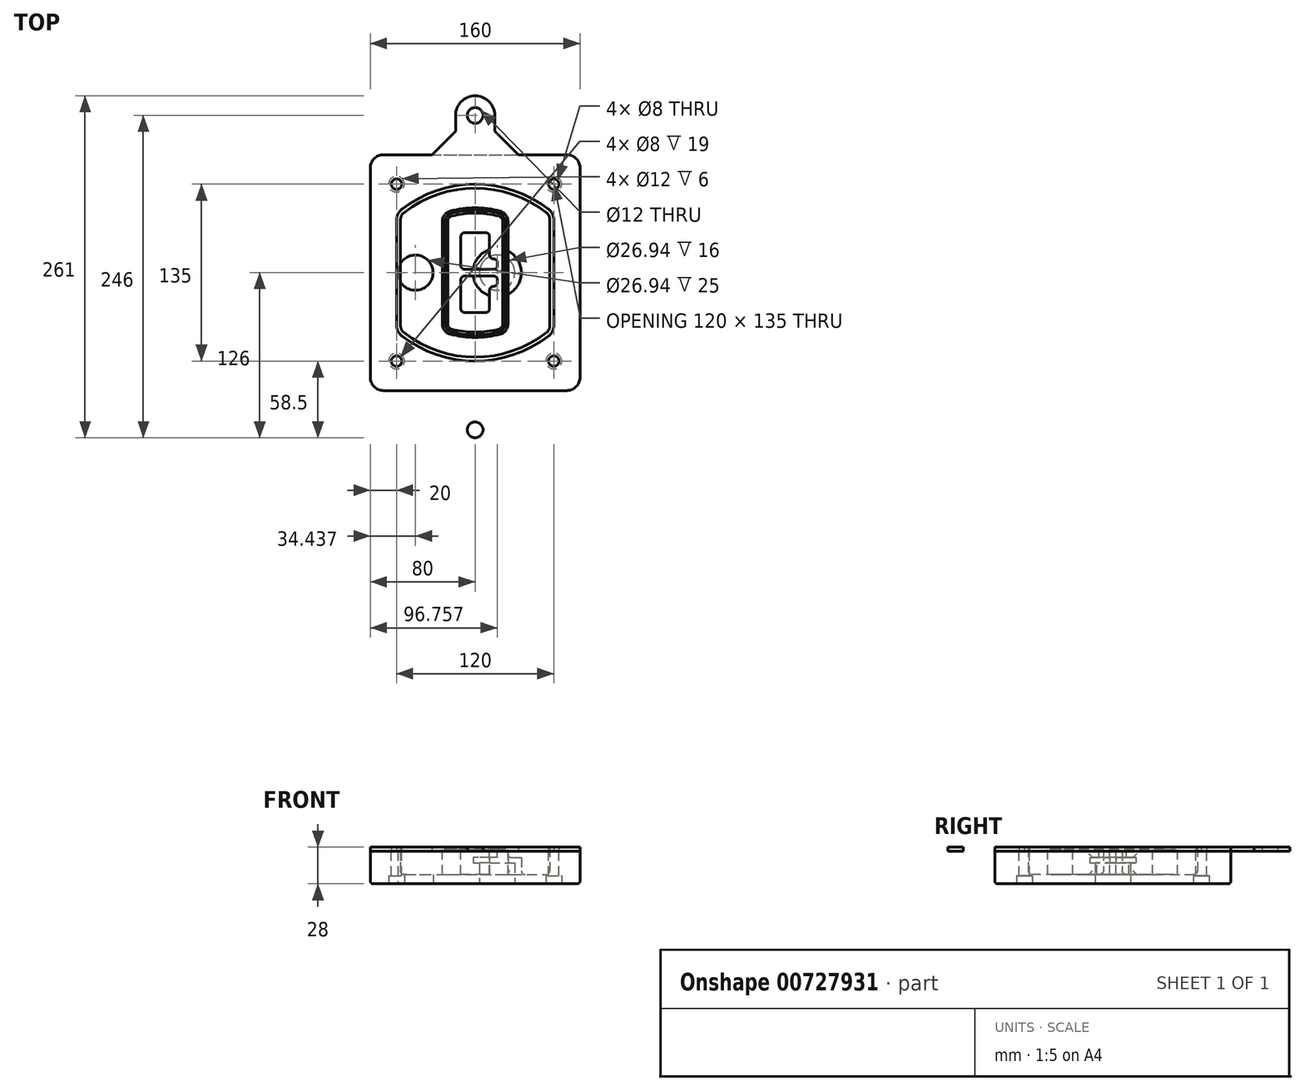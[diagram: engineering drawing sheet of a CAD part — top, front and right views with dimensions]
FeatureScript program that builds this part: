
annotation { "Feature Type Name" : "Feature", "Feature Type Description" : "" }
export const myFeature = defineFeature(function(context is Context, id is Id, definition is map)
    precondition{}
    {
        {
            var Q0;
            Q0=qCreatedBy(makeId("Top.planeOp"),FACE);
            var sketch = newSketch(context, id + "F0", { "sketchPlane" : qUnion([Q0])});
            skPoint(sketch, "E0.rect.middle", {"position": v(0, 0) * mm});
            skLineSegment(sketch, "E1.bottom", {"start": v(-70, -90) * mm, "end": v(70, -90) * mm});
            skLineSegment(sketch, "E1.top", {"start": v(-70, 90) * mm, "end": v(70, 90) * mm});
            skLineSegment(sketch, "E1.left", {"start": v(-80, -80) * mm, "end": v(-80, 80) * mm});
            skLineSegment(sketch, "E1.right", {"start": v(80, -80) * mm, "end": v(80, 80) * mm});
            skLineSegment(sketch, "E2", {"start": v(-80, 90) * mm, "end": v(80, -90) * mm, "construction": true});
            skLineSegment(sketch, "E3", {"start": v(80, 90) * mm, "end": v(-80, -90) * mm, "construction": true});
            skCircle(sketch, "E4", {"center": v(-60, 67.5) * mm, "radius": 4 * mm});
            skCircle(sketch, "E5", {"center": v(60, 67.5) * mm, "radius": 4 * mm});
            skCircle(sketch, "E6", {"center": v(60, -67.5) * mm, "radius": 4 * mm});
            skCircle(sketch, "E7", {"center": v(-60, -67.5) * mm, "radius": 4 * mm});
            skLineSegment(sketch, "E8", {"start": v(-60, 67.5) * mm, "end": v(60, 67.5) * mm, "construction": true});
            skLineSegment(sketch, "E9", {"start": v(60, 67.5) * mm, "end": v(60, -67.5) * mm, "construction": true});
            skLineSegment(sketch, "E10", {"start": v(60, -67.5) * mm, "end": v(-60, -67.5) * mm, "construction": true});
            skLineSegment(sketch, "E11", {"start": v(-60, -67.5) * mm, "end": v(-60, 67.5) * mm, "construction": true});
            skLineSegment(sketch, "E12", {"start": v(-60, 40.3) * mm, "end": v(-60, -40.3) * mm});
            skLineSegment(sketch, "E13", {"start": v(60, 40.3) * mm, "end": v(60, -40.3) * mm});
            skArc(sketch, "E14", {"start": v(56.15, 48.18) * mm, "mid": v(0, 67.5) * mm, "end": v(-56.15, 48.18) * mm});
            skArc(sketch, "E15", {"start": v(-56.15, -48.18) * mm, "mid": v(0, -67.5) * mm, "end": v(56.15, -48.18) * mm});
            skLineSegment(sketch, "E16", {"start": v(-60, 0) * mm, "end": v(60, 0) * mm, "construction": true});
            skPoint(sketch, "E17.visualSharp", {"position": v(-60, -45) * mm});
            skArc(sketch, "E17.filletArc", {"start": v(-60, -40.3) * mm, "mid": v(-58.99, -44.68) * mm, "end": v(-56.15, -48.18) * mm});
            skPoint(sketch, "E18.visualSharp", {"position": v(-60, 45) * mm});
            skArc(sketch, "E18.filletArc", {"start": v(-56.15, 48.18) * mm, "mid": v(-58.99, 44.68) * mm, "end": v(-60, 40.3) * mm});
            skPoint(sketch, "E19.visualSharp", {"position": v(60, 45) * mm});
            skArc(sketch, "E19.filletArc", {"start": v(60, 40.3) * mm, "mid": v(58.99, 44.68) * mm, "end": v(56.15, 48.18) * mm});
            skPoint(sketch, "E20.visualSharp", {"position": v(60, -45) * mm});
            skArc(sketch, "E20.filletArc", {"start": v(56.15, -48.18) * mm, "mid": v(58.99, -44.68) * mm, "end": v(60, -40.3) * mm});
            skPoint(sketch, "E21.visualSharp", {"position": v(-80, 90) * mm});
            skArc(sketch, "E21.filletArc", {"start": v(-70, 90) * mm, "mid": v(-77.07, 87.07) * mm, "end": v(-80, 80) * mm});
            skPoint(sketch, "E22.visualSharp", {"position": v(80, 90) * mm});
            skArc(sketch, "E22.filletArc", {"start": v(80, 80) * mm, "mid": v(77.07, 87.07) * mm, "end": v(70, 90) * mm});
            skPoint(sketch, "E23.visualSharp", {"position": v(80, -90) * mm});
            skArc(sketch, "E23.filletArc", {"start": v(70, -90) * mm, "mid": v(77.07, -87.07) * mm, "end": v(80, -80) * mm});
            skPoint(sketch, "E24.visualSharp", {"position": v(-80, -90) * mm});
            skArc(sketch, "E24.filletArc", {"start": v(-80, -80) * mm, "mid": v(-77.07, -87.07) * mm, "end": v(-70, -90) * mm});
            skArc(sketch, "E25.0", {"start": v(57, 40.3) * mm, "mid": v(56.3, 43.36) * mm, "end": v(54.3, 45.81) * mm});
            skLineSegment(sketch, "E25.1", {"start": v(57, 40.3) * mm, "end": v(57, -40.3) * mm});
            skArc(sketch, "E25.2", {"start": v(54.3, -45.81) * mm, "mid": v(56.3, -43.36) * mm, "end": v(57, -40.3) * mm});
            skArc(sketch, "E25.3", {"start": v(-54.3, -45.81) * mm, "mid": v(0, -64.5) * mm, "end": v(54.3, -45.81) * mm});
            skArc(sketch, "E25.4", {"start": v(-57, -40.3) * mm, "mid": v(-56.3, -43.36) * mm, "end": v(-54.3, -45.81) * mm});
            skArc(sketch, "E25.5", {"start": v(54.3, 45.81) * mm, "mid": v(0, 64.5) * mm, "end": v(-54.3, 45.81) * mm});
            skLineSegment(sketch, "E25.6", {"start": v(-57, 40.3) * mm, "end": v(-57, -40.3) * mm});
            skArc(sketch, "E25.7", {"start": v(-54.3, 45.81) * mm, "mid": v(-56.3, 43.36) * mm, "end": v(-57, 40.3) * mm});
            skArc(sketch, "E26.0", {"start": v(-58.62, 51.33) * mm, "mid": v(-62.58, 46.43) * mm, "end": v(-64, 40.3) * mm});
            skArc(sketch, "E26.1", {"start": v(58.62, 51.33) * mm, "mid": v(0, 71.5) * mm, "end": v(-58.62, 51.33) * mm});
            skArc(sketch, "E26.2", {"start": v(64, 40.3) * mm, "mid": v(62.58, 46.43) * mm, "end": v(58.62, 51.33) * mm});
            skLineSegment(sketch, "E26.3", {"start": v(64, 40.3) * mm, "end": v(64, -40.3) * mm});
            skArc(sketch, "E26.4", {"start": v(58.62, -51.33) * mm, "mid": v(62.58, -46.43) * mm, "end": v(64, -40.3) * mm});
            skLineSegment(sketch, "E26.5", {"start": v(-64, 40.3) * mm, "end": v(-64, -40.3) * mm});
            skArc(sketch, "E26.6", {"start": v(-58.62, -51.33) * mm, "mid": v(0, -71.5) * mm, "end": v(58.62, -51.33) * mm});
            skArc(sketch, "E26.7", {"start": v(-64, -40.3) * mm, "mid": v(-62.58, -46.43) * mm, "end": v(-58.62, -51.33) * mm});
            skSolve(sketch);
        }
        {
            var Q0;
            Q0=makeQuery(id+"F0.imprint","IMPRINT",FACE,{"disambiguationData":[TD([[makeQuery(id+"F0.imprint","IMPRINT",EDGE,{"derivedFrom":sQuery(id+"F0.wireOp",EDGE,"E1.bottom")}),1.0]])]});
            var Q1;
            Q1=makeQuery(id+"F0.imprint","IMPRINT",FACE,{"disambiguationData":[TD([[makeQuery(id+"F0.imprint","IMPRINT",EDGE,{"derivedFrom":sQuery(id+"F0.wireOp",EDGE,"E12")}),1.0]])]});
            var Q2;
            Q2=makeQuery(id+"F0.imprint","IMPRINT",FACE,{"disambiguationData":[TD([[makeQuery(id+"F0.imprint","IMPRINT",EDGE,{"derivedFrom":sQuery(id+"F0.wireOp",EDGE,"E25.0")}),1.0]])]});
            var Q3;
            Q3=makeQuery(id+"F0.imprint","IMPRINT",FACE,{"disambiguationData":[TD([[makeQuery(id+"F0.imprint","IMPRINT",EDGE,{"derivedFrom":sQuery(id+"F0.wireOp",EDGE,"E12")}),-1.0]])]});
            extrude(context, id + "F1", {"entities" : qUnion([Q0, Q1, Q2, Q3]), "oppositeDirection" : true, "depth" : 25 * mm});
        }
        {
            var Q0;
            Q0=makeQuery(id+"F0.imprint","IMPRINT",FACE,{"disambiguationData":[TD([[makeQuery(id+"F0.imprint","IMPRINT",EDGE,{"derivedFrom":sQuery(id+"F0.wireOp",EDGE,"E12")}),1.0]])]});
            extrude(context, id + "F2", {"entities" : qUnion([Q0]), "operationType" : NewBodyOperationType.ADD, "depth" : 3 * mm});
        }
        {
            var Q0;
            Q0=makeQuery(id+"F0.imprint","IMPRINT",FACE,{"disambiguationData":[TD([[makeQuery(id+"F0.imprint","IMPRINT",EDGE,{"derivedFrom":sQuery(id+"F0.wireOp",EDGE,"E25.0")}),1.0]])]});
            extrude(context, id + "F3", {"entities" : qUnion([Q0]), "operationType" : NewBodyOperationType.REMOVE, "oppositeDirection" : true, "depth" : 18 * mm});
        }
        {
            var Q0;
            Q0=makeQuery(id+"F2.opExtrude","CAP_FACE",FACE,{"disambiguationData":[OSD([sQuery(id+"F0.wireOp",EDGE,"E12"),sQuery(id+"F0.wireOp",EDGE,"E13"),sQuery(id+"F0.wireOp",EDGE,"E14"),sQuery(id+"F0.wireOp",EDGE,"E15"),sQuery(id+"F0.wireOp",EDGE,"E17.filletArc"),sQuery(id+"F0.wireOp",EDGE,"E18.filletArc"),sQuery(id+"F0.wireOp",EDGE,"E19.filletArc"),sQuery(id+"F0.wireOp",EDGE,"E20.filletArc"),sQuery(id+"F0.wireOp",EDGE,"E25.0"),sQuery(id+"F0.wireOp",EDGE,"E25.1"),sQuery(id+"F0.wireOp",EDGE,"E25.2"),sQuery(id+"F0.wireOp",EDGE,"E25.3"),sQuery(id+"F0.wireOp",EDGE,"E25.4"),sQuery(id+"F0.wireOp",EDGE,"E25.5"),sQuery(id+"F0.wireOp",EDGE,"E25.6"),sQuery(id+"F0.wireOp",EDGE,"E25.7")])],"isStart":false});
            var sketch = newSketch(context, id + "F4", { "sketchPlane" : qUnion([Q0])});
            skArc(sketch, "E27.0", {"start": v(-19.08, -46.97) * mm, "mid": v(0, -49.5) * mm, "end": v(19.08, -46.97) * mm});
            skArc(sketch, "E28.0", {"start": v(19.08, 46.97) * mm, "mid": v(0, 49.5) * mm, "end": v(-19.08, 46.97) * mm});
            skLineSegment(sketch, "E29", {"start": v(-25, 39.25) * mm, "end": v(-25, -39.25) * mm});
            skLineSegment(sketch, "E30", {"start": v(25, 39.25) * mm, "end": v(25, -39.25) * mm});
            skLineSegment(sketch, "E31", {"start": v(-25, 45.1) * mm, "end": v(25, 45.1) * mm, "construction": true});
            skLineSegment(sketch, "E32", {"start": v(-25, -45.1) * mm, "end": v(25, -45.1) * mm, "construction": true});
            skPoint(sketch, "E33.visualSharp", {"position": v(-25, 45.1) * mm});
            skArc(sketch, "E33.filletArc", {"start": v(-19.08, 46.97) * mm, "mid": v(-23.35, 44.11) * mm, "end": v(-25, 39.25) * mm});
            skPoint(sketch, "E34.visualSharp", {"position": v(25, 45.1) * mm});
            skArc(sketch, "E34.filletArc", {"start": v(25, 39.25) * mm, "mid": v(23.35, 44.11) * mm, "end": v(19.08, 46.97) * mm});
            skPoint(sketch, "E35.visualSharp", {"position": v(25, -45.1) * mm});
            skArc(sketch, "E35.filletArc", {"start": v(19.08, -46.97) * mm, "mid": v(23.35, -44.11) * mm, "end": v(25, -39.25) * mm});
            skPoint(sketch, "E36.visualSharp", {"position": v(-25, -45.1) * mm});
            skArc(sketch, "E36.filletArc", {"start": v(-25, -39.25) * mm, "mid": v(-23.35, -44.11) * mm, "end": v(-19.08, -46.97) * mm});
            skArc(sketch, "E37.0", {"start": v(54.3, 45.81) * mm, "mid": v(0, 64.5) * mm, "end": v(-54.3, 45.81) * mm});
            skArc(sketch, "E37.1", {"start": v(-54.3, 45.81) * mm, "mid": v(-56.3, 43.36) * mm, "end": v(-57, 40.3) * mm});
            skLineSegment(sketch, "E37.2", {"start": v(-57, 40.3) * mm, "end": v(-57, -40.3) * mm});
            skArc(sketch, "E37.3", {"start": v(-57, -40.3) * mm, "mid": v(-56.3, -43.36) * mm, "end": v(-54.3, -45.81) * mm});
            skArc(sketch, "E37.4", {"start": v(-54.3, -45.81) * mm, "mid": v(0, -64.5) * mm, "end": v(54.3, -45.81) * mm});
            skArc(sketch, "E37.5", {"start": v(54.3, -45.81) * mm, "mid": v(56.3, -43.36) * mm, "end": v(57, -40.3) * mm});
            skLineSegment(sketch, "E37.6", {"start": v(57, 40.3) * mm, "end": v(57, -40.3) * mm});
            skArc(sketch, "E37.7", {"start": v(57, 40.3) * mm, "mid": v(56.3, 43.36) * mm, "end": v(54.3, 45.81) * mm});
            skLineSegment(sketch, "E38.0", {"start": v(23, 39.25) * mm, "end": v(23, -39.25) * mm});
            skArc(sketch, "E38.1", {"start": v(18.56, -45.04) * mm, "mid": v(21.76, -42.9) * mm, "end": v(23, -39.25) * mm});
            skArc(sketch, "E38.2", {"start": v(-18.56, -45.04) * mm, "mid": v(0, -47.5) * mm, "end": v(18.56, -45.04) * mm});
            skArc(sketch, "E38.3", {"start": v(-23, -39.25) * mm, "mid": v(-21.76, -42.9) * mm, "end": v(-18.56, -45.04) * mm});
            skLineSegment(sketch, "E38.4", {"start": v(-23, 39.25) * mm, "end": v(-23, -39.25) * mm});
            skArc(sketch, "E38.5", {"start": v(23, 39.25) * mm, "mid": v(21.76, 42.9) * mm, "end": v(18.56, 45.04) * mm});
            skArc(sketch, "E38.6", {"start": v(-18.56, 45.04) * mm, "mid": v(-21.76, 42.9) * mm, "end": v(-23, 39.25) * mm});
            skArc(sketch, "E38.7", {"start": v(18.56, 45.04) * mm, "mid": v(0, 47.5) * mm, "end": v(-18.56, 45.04) * mm});
            skArc(sketch, "E39.0", {"start": v(21, 39.25) * mm, "mid": v(20.18, 41.68) * mm, "end": v(18.04, 43.1) * mm});
            skLineSegment(sketch, "E39.1", {"start": v(21, 39.25) * mm, "end": v(21, -39.25) * mm});
            skArc(sketch, "E39.2", {"start": v(18.04, -43.1) * mm, "mid": v(20.18, -41.68) * mm, "end": v(21, -39.25) * mm});
            skArc(sketch, "E39.3", {"start": v(-18.04, -43.1) * mm, "mid": v(0, -45.5) * mm, "end": v(18.04, -43.1) * mm});
            skArc(sketch, "E39.4", {"start": v(-21, -39.25) * mm, "mid": v(-20.18, -41.68) * mm, "end": v(-18.04, -43.1) * mm});
            skArc(sketch, "E39.5", {"start": v(18.04, 43.1) * mm, "mid": v(0, 45.5) * mm, "end": v(-18.04, 43.1) * mm});
            skLineSegment(sketch, "E39.6", {"start": v(-21, 39.25) * mm, "end": v(-21, -39.25) * mm});
            skArc(sketch, "E39.7", {"start": v(-18.04, 43.1) * mm, "mid": v(-20.18, 41.68) * mm, "end": v(-21, 39.25) * mm});
            skLineSegment(sketch, "E40", {"start": v(-25, 0) * mm, "end": v(25, 0) * mm, "construction": true});
            skLineSegment(sketch, "E41", {"start": v(-11, 5.5) * mm, "end": v(-11, 27.5) * mm});
            skLineSegment(sketch, "E42", {"start": v(-8, 30.5) * mm, "end": v(8, 30.5) * mm});
            skLineSegment(sketch, "E43", {"start": v(11, 27.5) * mm, "end": v(11, 13.5) * mm});
            skLineSegment(sketch, "E44", {"start": v(14, 10.5) * mm, "end": v(14, 10.5) * mm});
            skLineSegment(sketch, "E45", {"start": v(17, 7.5) * mm, "end": v(17, 5.5) * mm});
            skLineSegment(sketch, "E46", {"start": v(14, 2.5) * mm, "end": v(-8, 2.5) * mm});
            skPoint(sketch, "E47.visualSharp", {"position": v(-11, 30.5) * mm});
            skArc(sketch, "E47.filletArc", {"start": v(-8, 30.5) * mm, "mid": v(-10.12, 29.62) * mm, "end": v(-11, 27.5) * mm});
            skPoint(sketch, "E48.visualSharp", {"position": v(11, 30.5) * mm});
            skArc(sketch, "E48.filletArc", {"start": v(11, 27.5) * mm, "mid": v(10.12, 29.62) * mm, "end": v(8, 30.5) * mm});
            skPoint(sketch, "E49.visualSharp", {"position": v(11, 10.5) * mm});
            skArc(sketch, "E49.filletArc", {"start": v(11, 13.5) * mm, "mid": v(11.88, 11.38) * mm, "end": v(14, 10.5) * mm});
            skPoint(sketch, "E50.visualSharp", {"position": v(17, 10.5) * mm});
            skArc(sketch, "E50.filletArc", {"start": v(17, 7.5) * mm, "mid": v(16.12, 9.62) * mm, "end": v(14, 10.5) * mm});
            skPoint(sketch, "E51.visualSharp", {"position": v(17, 2.5) * mm});
            skArc(sketch, "E51.filletArc", {"start": v(14, 2.5) * mm, "mid": v(16.12, 3.38) * mm, "end": v(17, 5.5) * mm});
            skPoint(sketch, "E52.visualSharp", {"position": v(-11, 2.5) * mm});
            skArc(sketch, "E52.filletArc", {"start": v(-11, 5.5) * mm, "mid": v(-10.12, 3.38) * mm, "end": v(-8, 2.5) * mm});
            skLineSegment(sketch, "E53.0.MirrorCS", {"start": v(14, -2.5) * mm, "end": v(-8, -2.5) * mm});
            skArc(sketch, "E54.0.MirrorCS", {"start": v(-11, -5.5) * mm, "mid": v(-10.12, -3.38) * mm, "end": v(-8, -2.5) * mm});
            skLineSegment(sketch, "E55.0.MirrorCS", {"start": v(-11, -5.5) * mm, "end": v(-11, -27.5) * mm});
            skArc(sketch, "E56.0.MirrorCS", {"start": v(-8, -30.5) * mm, "mid": v(-10.12, -29.62) * mm, "end": v(-11, -27.5) * mm});
            skLineSegment(sketch, "E57.0.MirrorCS", {"start": v(-8, -30.5) * mm, "end": v(8, -30.5) * mm});
            skArc(sketch, "E58.0.MirrorCS", {"start": v(11, -27.5) * mm, "mid": v(10.12, -29.62) * mm, "end": v(8, -30.5) * mm});
            skLineSegment(sketch, "E59.0.MirrorCS", {"start": v(11, -27.5) * mm, "end": v(11, -13.5) * mm});
            skArc(sketch, "E60.0.MirrorCS", {"start": v(11, -13.5) * mm, "mid": v(11.88, -11.38) * mm, "end": v(14, -10.5) * mm});
            skArc(sketch, "E61.0.MirrorCS", {"start": v(17, -7.5) * mm, "mid": v(16.12, -9.62) * mm, "end": v(14, -10.5) * mm});
            skLineSegment(sketch, "E62.0.MirrorCS", {"start": v(17, -7.5) * mm, "end": v(17, -5.5) * mm});
            skArc(sketch, "E63.0.MirrorCS", {"start": v(14, -2.5) * mm, "mid": v(16.12, -3.38) * mm, "end": v(17, -5.5) * mm});
            skSolve(sketch);
        }
        {
            var Q0;
            Q0=makeQuery(id+"F4.imprint","IMPRINT",FACE,{"disambiguationData":[TD([[makeQuery(id+"F4.imprint","IMPRINT",EDGE,{"derivedFrom":sQuery(id+"F4.wireOp",EDGE,"E27.0")}),1.0]])]});
            var Q1;
            Q1=makeQuery(id+"F4.imprint","IMPRINT",FACE,{"disambiguationData":[TD([[makeQuery(id+"F4.imprint","IMPRINT",EDGE,{"derivedFrom":sQuery(id+"F4.wireOp",EDGE,"E38.0")}),-1.0]])]});
            var Q2;
            Q2=makeQuery(id+"F4.imprint","IMPRINT",FACE,{"disambiguationData":[TD([[makeQuery(id+"F4.imprint","IMPRINT",EDGE,{"derivedFrom":sQuery(id+"F4.wireOp",EDGE,"E39.0")}),1.0]])]});
            extrude(context, id + "F5", {"entities" : qUnion([Q0, Q1, Q2]), "operationType" : NewBodyOperationType.ADD, "endBound" : BoundingType.UP_TO_NEXT, "oppositeDirection" : true, "depth" : 25 * mm});
        }
        {
            var Q0;
            Q0=makeQuery(id+"F4.imprint","IMPRINT",FACE,{"disambiguationData":[TD([[makeQuery(id+"F4.imprint","IMPRINT",EDGE,{"derivedFrom":sQuery(id+"F4.wireOp",EDGE,"E38.0")}),-1.0]])]});
            extrude(context, id + "F6", {"entities" : qUnion([Q0]), "operationType" : NewBodyOperationType.REMOVE, "oppositeDirection" : true, "depth" : 2 * mm});
        }
        {
            var Q0;
            Q0=makeQuery(id+"F1.opExtrude","CAP_FACE",FACE,{"disambiguationData":[OSD([sQuery(id+"F0.wireOp",EDGE,"E1.bottom"),sQuery(id+"F0.wireOp",EDGE,"E1.top"),sQuery(id+"F0.wireOp",EDGE,"E1.left"),sQuery(id+"F0.wireOp",EDGE,"E1.right"),sQuery(id+"F0.wireOp",EDGE,"E4"),sQuery(id+"F0.wireOp",EDGE,"E5"),sQuery(id+"F0.wireOp",EDGE,"E6"),sQuery(id+"F0.wireOp",EDGE,"E7"),sQuery(id+"F0.wireOp",EDGE,"E21.filletArc"),sQuery(id+"F0.wireOp",EDGE,"E22.filletArc"),sQuery(id+"F0.wireOp",EDGE,"E23.filletArc"),sQuery(id+"F0.wireOp",EDGE,"E24.filletArc")])],"isStart":false});
            var sketch = newSketch(context, id + "F7", { "sketchPlane" : qUnion([Q0])});
            skCircle(sketch, "E64", {"center": v(16.76, 0) * mm, "radius": 13.47 * mm});
            skCircle(sketch, "E65", {"center": v(-45.56, 0) * mm, "radius": 13.47 * mm});
            skLineSegment(sketch, "E66", {"start": v(80, 0) * mm, "end": v(-80, 0) * mm});
            skCircle(sketch, "E67", {"center": v(16.76, 0) * mm, "radius": 18.47 * mm});
            skCircle(sketch, "E68", {"center": v(60, -67.5) * mm, "radius": 6 * mm});
            skCircle(sketch, "E69", {"center": v(-60, -67.5) * mm, "radius": 6 * mm});
            skCircle(sketch, "E70", {"center": v(-60, 67.5) * mm, "radius": 6 * mm});
            skCircle(sketch, "E71", {"center": v(60, 67.5) * mm, "radius": 6 * mm});
            skSolve(sketch);
        }
        {
            var Q0;
            {var subQ1=sQuery(id+"F7.wireOp",EDGE,"E66");var subQ4=sQuery(id+"F7.wireOp",EDGE,"E64");var subQ6=makeQuery(id+"F7.imprint","INTERSECT",VERTEX,{"disambiguationData":[OD(0.0)],"derivedFrom":[subQ4,subQ1]});Q0=makeQuery(id+"F7.imprint","IMPRINT",FACE,{"disambiguationData":[TD([[makeQuery(id+"F7.imprint","IMPRINT",EDGE,{"disambiguationData":[TD([[subQ6,-1.0]])],"derivedFrom":subQ4}),-1.0]])]});}
            var Q1;
            {var subQ0=sQuery(id+"F7.wireOp",EDGE,"E66");var subQ1=sQuery(id+"F7.wireOp",EDGE,"E64");var subQ3=makeQuery(id+"F7.imprint","INTERSECT",VERTEX,{"disambiguationData":[OD(0.0)],"derivedFrom":[subQ1,subQ0]});Q1=makeQuery(id+"F7.imprint","IMPRINT",FACE,{"disambiguationData":[TD([[makeQuery(id+"F7.imprint","IMPRINT",EDGE,{"disambiguationData":[TD([[subQ3,-1.0]])],"derivedFrom":subQ1}),1.0]])]});}
            var Q2;
            {var subQ0=sQuery(id+"F7.wireOp",EDGE,"E66");var subQ1=sQuery(id+"F7.wireOp",EDGE,"E64");var subQ3=makeQuery(id+"F7.imprint","INTERSECT",VERTEX,{"disambiguationData":[OD(0.0)],"derivedFrom":[subQ1,subQ0]});Q2=makeQuery(id+"F7.imprint","IMPRINT",FACE,{"disambiguationData":[TD([[makeQuery(id+"F7.imprint","IMPRINT",EDGE,{"disambiguationData":[TD([[subQ3,1.0]])],"derivedFrom":subQ1}),1.0]])]});}
            var Q3;
            {var subQ1=sQuery(id+"F7.wireOp",EDGE,"E66");var subQ4=sQuery(id+"F7.wireOp",EDGE,"E64");var subQ6=makeQuery(id+"F7.imprint","INTERSECT",VERTEX,{"disambiguationData":[OD(0.0)],"derivedFrom":[subQ4,subQ1]});Q3=makeQuery(id+"F7.imprint","IMPRINT",FACE,{"disambiguationData":[TD([[makeQuery(id+"F7.imprint","IMPRINT",EDGE,{"disambiguationData":[TD([[subQ6,1.0]])],"derivedFrom":subQ4}),-1.0]])]});}
            extrude(context, id + "F8", {"entities" : qUnion([Q0, Q1, Q2, Q3]), "operationType" : NewBodyOperationType.ADD, "oppositeDirection" : true, "depth" : 20 * mm});
        }
        {
            var Q0;
            {var subQ0=sQuery(id+"F7.wireOp",EDGE,"E66");var subQ1=sQuery(id+"F7.wireOp",EDGE,"E64");var subQ3=makeQuery(id+"F7.imprint","INTERSECT",VERTEX,{"disambiguationData":[OD(0.0)],"derivedFrom":[subQ1,subQ0]});Q0=makeQuery(id+"F7.imprint","IMPRINT",FACE,{"disambiguationData":[TD([[makeQuery(id+"F7.imprint","IMPRINT",EDGE,{"disambiguationData":[TD([[subQ3,-1.0]])],"derivedFrom":subQ1}),1.0]])]});}
            var Q1;
            {var subQ0=sQuery(id+"F7.wireOp",EDGE,"E66");var subQ1=sQuery(id+"F7.wireOp",EDGE,"E64");var subQ3=makeQuery(id+"F7.imprint","INTERSECT",VERTEX,{"disambiguationData":[OD(0.0)],"derivedFrom":[subQ1,subQ0]});Q1=makeQuery(id+"F7.imprint","IMPRINT",FACE,{"disambiguationData":[TD([[makeQuery(id+"F7.imprint","IMPRINT",EDGE,{"disambiguationData":[TD([[subQ3,1.0]])],"derivedFrom":subQ1}),1.0]])]});}
            extrude(context, id + "F9", {"entities" : qUnion([Q0, Q1]), "operationType" : NewBodyOperationType.REMOVE, "oppositeDirection" : true, "depth" : 16 * mm});
        }
        {
            var Q0;
            {var subQ0=sQuery(id+"F7.wireOp",EDGE,"E66");var subQ1=sQuery(id+"F7.wireOp",EDGE,"E65");var subQ3=makeQuery(id+"F7.imprint","INTERSECT",VERTEX,{"disambiguationData":[OD(0.0)],"derivedFrom":[subQ1,subQ0]});Q0=makeQuery(id+"F7.imprint","IMPRINT",FACE,{"disambiguationData":[TD([[makeQuery(id+"F7.imprint","IMPRINT",EDGE,{"disambiguationData":[TD([[subQ3,-1.0]])],"derivedFrom":subQ1}),1.0]])]});}
            var Q1;
            {var subQ0=sQuery(id+"F7.wireOp",EDGE,"E66");var subQ1=sQuery(id+"F7.wireOp",EDGE,"E65");var subQ3=makeQuery(id+"F7.imprint","INTERSECT",VERTEX,{"disambiguationData":[OD(0.0)],"derivedFrom":[subQ1,subQ0]});Q1=makeQuery(id+"F7.imprint","IMPRINT",FACE,{"disambiguationData":[TD([[makeQuery(id+"F7.imprint","IMPRINT",EDGE,{"disambiguationData":[TD([[subQ3,1.0]])],"derivedFrom":subQ1}),1.0]])]});}
            extrude(context, id + "F10", {"entities" : qUnion([Q0, Q1]), "operationType" : NewBodyOperationType.REMOVE, "oppositeDirection" : true, "depth" : 25 * mm});
        }
        {
            var Q0;
            Q0=makeQuery(id+"F7.imprint","IMPRINT",FACE,{"disambiguationData":[TD([[makeQuery(id+"F7.imprint","IMPRINT",EDGE,{"derivedFrom":sQuery(id+"F7.wireOp",EDGE,"E68")}),1.0]])]});
            var Q1;
            Q1=makeQuery(id+"F7.imprint","IMPRINT",FACE,{"disambiguationData":[TD([[makeQuery(id+"F7.imprint","IMPRINT",EDGE,{"derivedFrom":makeQuery(id+"F1.opExtrude","CAP_EDGE",EDGE,{"disambiguationData":[OSD([sQuery(id+"F0.wireOp",EDGE,"E5")])],"isStart":false})}),-1.0]])]});
            var Q2;
            Q2=makeQuery(id+"F7.imprint","IMPRINT",FACE,{"disambiguationData":[TD([[makeQuery(id+"F7.imprint","IMPRINT",EDGE,{"derivedFrom":sQuery(id+"F7.wireOp",EDGE,"E69")}),1.0]])]});
            var Q3;
            Q3=makeQuery(id+"F7.imprint","IMPRINT",FACE,{"disambiguationData":[TD([[makeQuery(id+"F7.imprint","IMPRINT",EDGE,{"derivedFrom":makeQuery(id+"F1.opExtrude","CAP_EDGE",EDGE,{"disambiguationData":[OSD([sQuery(id+"F0.wireOp",EDGE,"E4")])],"isStart":false})}),-1.0]])]});
            var Q4;
            Q4=makeQuery(id+"F7.imprint","IMPRINT",FACE,{"disambiguationData":[TD([[makeQuery(id+"F7.imprint","IMPRINT",EDGE,{"derivedFrom":sQuery(id+"F7.wireOp",EDGE,"E70")}),1.0]])]});
            var Q5;
            Q5=makeQuery(id+"F7.imprint","IMPRINT",FACE,{"disambiguationData":[TD([[makeQuery(id+"F7.imprint","IMPRINT",EDGE,{"derivedFrom":makeQuery(id+"F1.opExtrude","CAP_EDGE",EDGE,{"disambiguationData":[OSD([sQuery(id+"F0.wireOp",EDGE,"E7")])],"isStart":false})}),-1.0]])]});
            var Q6;
            Q6=makeQuery(id+"F7.imprint","IMPRINT",FACE,{"disambiguationData":[TD([[makeQuery(id+"F7.imprint","IMPRINT",EDGE,{"derivedFrom":sQuery(id+"F7.wireOp",EDGE,"E71")}),1.0]])]});
            var Q7;
            Q7=makeQuery(id+"F7.imprint","IMPRINT",FACE,{"disambiguationData":[TD([[makeQuery(id+"F7.imprint","IMPRINT",EDGE,{"derivedFrom":makeQuery(id+"F1.opExtrude","CAP_EDGE",EDGE,{"disambiguationData":[OSD([sQuery(id+"F0.wireOp",EDGE,"E6")])],"isStart":false})}),-1.0]])]});
            extrude(context, id + "F11", {"entities" : qUnion([Q0, Q1, Q2, Q3, Q4, Q5, Q6, Q7]), "operationType" : NewBodyOperationType.REMOVE, "oppositeDirection" : true, "depth" : 6 * mm});
        }
        {
            var Q0;
            Q0=makeQuery(id+"F9.boolean.opBoolean","COPY",FACE,{"derivedFrom":makeQuery(id+"F9.opExtrude","CAP_FACE",FACE,{"disambiguationData":[OSD([sQuery(id+"F7.wireOp",EDGE,"E64")])],"isStart":false})});
            var sketch = newSketch(context, id + "F12", { "sketchPlane" : qUnion([Q0])});
            skArc(sketch, "E72.0", {"start": v(11, 17.55) * mm, "mid": v(2.57, 11.82) * mm, "end": v(-1.54, 2.5) * mm});
            skArc(sketch, "E72.1", {"start": v(-1.54, -2.5) * mm, "mid": v(2.57, -11.82) * mm, "end": v(11, -17.55) * mm});
            skLineSegment(sketch, "E73", {"start": v(-1.54, -2.5) * mm, "end": v(14, -2.5) * mm});
            skLineSegment(sketch, "E74.0", {"start": v(14, 2.5) * mm, "end": v(-1.54, 2.5) * mm});
            skArc(sketch, "E74.1", {"start": v(14, 2.5) * mm, "mid": v(16.12, 3.38) * mm, "end": v(17, 5.5) * mm});
            skLineSegment(sketch, "E74.2", {"start": v(17, 7.5) * mm, "end": v(17, 5.5) * mm});
            skArc(sketch, "E74.3", {"start": v(17, 7.5) * mm, "mid": v(16.12, 9.62) * mm, "end": v(14, 10.5) * mm});
            skArc(sketch, "E74.4", {"start": v(11, 13.5) * mm, "mid": v(11.88, 11.38) * mm, "end": v(14, 10.5) * mm});
            skLineSegment(sketch, "E74.5", {"start": v(11, 17.55) * mm, "end": v(11, 13.5) * mm});
            skLineSegment(sketch, "E74.7", {"start": v(14, -2.5) * mm, "end": v(-1.54, -2.5) * mm});
            skArc(sketch, "E74.8", {"start": v(14, -2.5) * mm, "mid": v(16.12, -3.38) * mm, "end": v(17, -5.5) * mm});
            skLineSegment(sketch, "E74.9", {"start": v(17, -7.5) * mm, "end": v(17, -5.5) * mm});
            skArc(sketch, "E74.10", {"start": v(17, -7.5) * mm, "mid": v(16.12, -9.62) * mm, "end": v(14, -10.5) * mm});
            skArc(sketch, "E74.11", {"start": v(11, -13.5) * mm, "mid": v(11.88, -11.38) * mm, "end": v(14, -10.5) * mm});
            skLineSegment(sketch, "E74.12", {"start": v(11, -17.55) * mm, "end": v(11, -13.5) * mm});
            skPoint(sketch, "E75.orphan", {"position": v(11, -27.5) * mm});
            skPoint(sketch, "E76.orphan", {"position": v(-8, -2.5) * mm});
            skPoint(sketch, "E77.orphan", {"position": v(-8, 2.5) * mm});
            skPoint(sketch, "E78.orphan", {"position": v(11, 27.5) * mm});
            skSolve(sketch);
        }
        {
            var Q0;
            {var subQ7=sQuery(id+"F12.wireOp",EDGE,"E72.0");var subQ14=sQuery(id+"F12.wireOp",EDGE,"E72.1");var subQ16=sQuery(id+"F12.wireOp",EDGE,"E74.1");var subQ18=sQuery(id+"F12.wireOp",EDGE,"E74.8");Q0=qUnion([makeQuery(id+"F12.imprint","IMPRINT",FACE,{"disambiguationData":[TD([[makeQuery(id+"F12.imprint","IMPRINT",EDGE,{"derivedFrom":subQ7}),1.0]])]}),makeQuery(id+"F12.imprint","IMPRINT",FACE,{"disambiguationData":[TD([[makeQuery(id+"F12.imprint","IMPRINT",EDGE,{"derivedFrom":subQ14}),1.0]])]}),makeQuery(id+"F12.imprint","IMPRINT",FACE,{"disambiguationData":[TD([[makeQuery(id+"F12.imprint","IMPRINT",EDGE,{"derivedFrom":subQ16}),1.0]])]}),makeQuery(id+"F12.imprint","IMPRINT",FACE,{"disambiguationData":[TD([[makeQuery(id+"F12.imprint","IMPRINT",EDGE,{"derivedFrom":subQ18}),-1.0]])]})]);}
            var Q1;
            Q1=makeQuery(id+"F5.boolean.opBoolean","SPLIT",FACE,{"disambiguationData":[TD([makeQuery(id+"F5.opExtrude","SWEPT_FACE",FACE,{"disambiguationData":[OSD([sQuery(id+"F4.wireOp",EDGE,"E41")])]})])],"derivedFrom":makeQuery(id+"F3.boolean.opBoolean","COPY",FACE,{"derivedFrom":makeQuery(id+"F3.opExtrude","CAP_FACE",FACE,{"disambiguationData":[OSD([sQuery(id+"F0.wireOp",EDGE,"E25.0"),sQuery(id+"F0.wireOp",EDGE,"E25.1"),sQuery(id+"F0.wireOp",EDGE,"E25.2"),sQuery(id+"F0.wireOp",EDGE,"E25.3"),sQuery(id+"F0.wireOp",EDGE,"E25.4"),sQuery(id+"F0.wireOp",EDGE,"E25.5"),sQuery(id+"F0.wireOp",EDGE,"E25.6"),sQuery(id+"F0.wireOp",EDGE,"E25.7")])],"isStart":false})})});
            extrude(context, id + "F13", {"entities" : qUnion([Q0]), "operationType" : NewBodyOperationType.REMOVE, "endBound" : BoundingType.UP_TO_SURFACE, "endBoundEntityFace" : qUnion([Q1]), "depth" : 25 * mm});
        }
        {
            var Q0;
            Q0=makeQuery(id+"F3.boolean.opBoolean","COPY",EDGE,{"derivedFrom":makeQuery(id+"F3.opExtrude","CAP_EDGE",EDGE,{"disambiguationData":[OSD([sQuery(id+"F0.wireOp",EDGE,"E25.6")])],"isStart":false})});
            var Q1;
            Q1=makeQuery(id+"F8.boolean.opBoolean","INTERSECT",EDGE,{"derivedFrom":[makeQuery(id+"F5.opExtrude","SWEPT_FACE",FACE,{"disambiguationData":[OSD([sQuery(id+"F4.wireOp",EDGE,"E30")])]}),makeQuery(id+"F8.opExtrude","CAP_FACE",FACE,{"disambiguationData":[OSD([sQuery(id+"F7.wireOp",EDGE,"E67")])],"isStart":false})]});
            var Q2;
            Q2=makeQuery(id+"F8.boolean.opBoolean","INTERSECT",EDGE,{"disambiguationData":[OD(1.0)],"derivedFrom":[makeQuery(id+"F5.opExtrude","SWEPT_FACE",FACE,{"disambiguationData":[OSD([sQuery(id+"F4.wireOp",EDGE,"E30")])]}),makeQuery(id+"F8.opExtrude","SWEPT_FACE",FACE,{"disambiguationData":[OSD([sQuery(id+"F7.wireOp",EDGE,"E67")])]})]});
            var Q3;
            {var subQ0=makeQuery(id+"F3.boolean.opBoolean","COPY",FACE,{"derivedFrom":makeQuery(id+"F3.opExtrude","CAP_FACE",FACE,{"disambiguationData":[OSD([sQuery(id+"F0.wireOp",EDGE,"E25.0"),sQuery(id+"F0.wireOp",EDGE,"E25.1"),sQuery(id+"F0.wireOp",EDGE,"E25.2"),sQuery(id+"F0.wireOp",EDGE,"E25.3"),sQuery(id+"F0.wireOp",EDGE,"E25.4"),sQuery(id+"F0.wireOp",EDGE,"E25.5"),sQuery(id+"F0.wireOp",EDGE,"E25.6"),sQuery(id+"F0.wireOp",EDGE,"E25.7")])],"isStart":false})});var subQ1=sQuery(id+"F4.wireOp",EDGE,"E30");Q3=makeQuery(id+"F8.boolean.opBoolean","SPLIT",EDGE,{"disambiguationData":[TD([makeQuery(id+"F5.opExtrude","SWEPT_FACE",FACE,{"disambiguationData":[OSD([sQuery(id+"F4.wireOp",EDGE,"E35.filletArc")])]})])],"derivedFrom":makeQuery(id+"F5.opExtrude","TWEAK_EDGE",EDGE,{"derivedFrom":[subQ0,makeQuery(id+"F4.imprint","IMPRINT",EDGE,{"derivedFrom":subQ1})]})});}
            var Q4;
            {var subQ0=sQuery(id+"F0.wireOp",EDGE,"E25.0");var subQ1=sQuery(id+"F0.wireOp",EDGE,"E25.1");var subQ2=sQuery(id+"F0.wireOp",EDGE,"E25.2");var subQ3=sQuery(id+"F0.wireOp",EDGE,"E25.3");var subQ4=sQuery(id+"F0.wireOp",EDGE,"E25.4");var subQ5=sQuery(id+"F0.wireOp",EDGE,"E25.5");var subQ6=sQuery(id+"F0.wireOp",EDGE,"E25.6");var subQ7=sQuery(id+"F0.wireOp",EDGE,"E25.7");Q4=makeQuery(id+"F8.boolean.opBoolean","INTERSECT",EDGE,{"derivedFrom":[makeQuery(id+"F5.boolean.opBoolean","SPLIT",FACE,{"disambiguationData":[TD([makeQuery(id+"F2.opExtrude","SWEPT_FACE",FACE,{"disambiguationData":[OSD([subQ0])]})])],"derivedFrom":makeQuery(id+"F3.boolean.opBoolean","COPY",FACE,{"derivedFrom":makeQuery(id+"F3.opExtrude","CAP_FACE",FACE,{"disambiguationData":[OSD([subQ0,subQ1,subQ2,subQ3,subQ4,subQ5,subQ6,subQ7])],"isStart":false})})}),makeQuery(id+"F8.opExtrude","SWEPT_FACE",FACE,{"disambiguationData":[OSD([sQuery(id+"F7.wireOp",EDGE,"E67")])]})]});}
            var Q5;
            Q5=makeQuery(id+"F8.boolean.opBoolean","INTERSECT",EDGE,{"disambiguationData":[OD(0.0)],"derivedFrom":[makeQuery(id+"F5.opExtrude","SWEPT_FACE",FACE,{"disambiguationData":[OSD([sQuery(id+"F4.wireOp",EDGE,"E30")])]}),makeQuery(id+"F8.opExtrude","SWEPT_FACE",FACE,{"disambiguationData":[OSD([sQuery(id+"F7.wireOp",EDGE,"E67")])]})]});
            fillet(context, id + "F14", {"entities" : qUnion([Q0, Q1, Q2, Q3, Q4, Q5]), "radius" : 3 * mm, "tangentPropagation" : true, "allowEdgeOverflow" : false});
        }
        {
            var Q0;
            Q0=makeQuery(id+"F1.opExtrude","CAP_EDGE",EDGE,{"disambiguationData":[OSD([sQuery(id+"F0.wireOp",EDGE,"E1.bottom")])],"isStart":false});
            fillet(context, id + "F15", {"entities" : qUnion([Q0]), "radius" : 2 * mm, "tangentPropagation" : true, "allowEdgeOverflow" : false});
        }
        {
            var Q0;
            {var subQ0=sQuery(id+"F0.wireOp",EDGE,"E21.filletArc");var subQ1=sQuery(id+"F0.wireOp",EDGE,"E7");var subQ2=sQuery(id+"F0.wireOp",EDGE,"E6");var subQ3=sQuery(id+"F0.wireOp",EDGE,"E5");var subQ4=sQuery(id+"F0.wireOp",EDGE,"E4");var subQ5=sQuery(id+"F0.wireOp",EDGE,"E22.filletArc");var subQ6=sQuery(id+"F0.wireOp",EDGE,"E1.bottom");var subQ7=sQuery(id+"F0.wireOp",EDGE,"E1.right");var subQ8=sQuery(id+"F0.wireOp",EDGE,"E1.top");var subQ9=sQuery(id+"F0.wireOp",EDGE,"E1.left");var subQ10=sQuery(id+"F0.wireOp",EDGE,"E23.filletArc");var subQ11=sQuery(id+"F0.wireOp",EDGE,"E24.filletArc");Q0=makeQuery(id+"F2.boolean.opBoolean","SPLIT",FACE,{"disambiguationData":[TD([makeQuery(id+"F1.opExtrude","SWEPT_FACE",FACE,{"disambiguationData":[OSD([subQ6])]})])],"derivedFrom":makeQuery(id+"F1.opExtrude","CAP_FACE",FACE,{"disambiguationData":[OSD([subQ6,subQ8,subQ9,subQ7,subQ4,subQ3,subQ2,subQ1,subQ0,subQ5,subQ10,subQ11])],"isStart":true})});}
            var sketch = newSketch(context, id + "F16", { "sketchPlane" : qUnion([Q0])});
            skLineSegment(sketch, "E79", {"start": v(0, 90) * mm, "end": v(0, 120) * mm, "construction": true});
            skLineSegment(sketch, "E80", {"start": v(-33, 90) * mm, "end": v(-15, 108) * mm});
            skLineSegment(sketch, "E81", {"start": v(33, 90) * mm, "end": v(15, 108) * mm});
            skCircle(sketch, "E82", {"center": v(0, 120) * mm, "radius": 6 * mm});
            skLineSegment(sketch, "E83", {"start": v(15, 108) * mm, "end": v(15, 120) * mm});
            skLineSegment(sketch, "E84", {"start": v(-15, 108) * mm, "end": v(-15, 120) * mm});
            skArc(sketch, "E85", {"start": v(15, 120) * mm, "mid": v(0, 135) * mm, "end": v(-15, 120) * mm});
            skLineSegment(sketch, "E86", {"start": v(-80, 0) * mm, "end": v(80, 0) * mm, "construction": true});
            skCircle(sketch, "E87.MirrorC", {"center": v(0, -120) * mm, "radius": 6 * mm});
            skLineSegment(sketch, "E88.MirrorCS", {"start": v(33, -90) * mm, "end": v(15, -108) * mm});
            skLineSegment(sketch, "E89.MirrorCS", {"start": v(-33, -90) * mm, "end": v(-15, -108) * mm});
            skLineSegment(sketch, "E90.MirrorCS", {"start": v(-15, -108) * mm, "end": v(-15, -120) * mm});
            skArc(sketch, "E91.MirrorCS", {"start": v(15, -120) * mm, "mid": v(0, -135) * mm, "end": v(-15, -120) * mm});
            skLineSegment(sketch, "E92.MirrorCS", {"start": v(15, -108) * mm, "end": v(15, -120) * mm});
            skLineSegment(sketch, "E93.MirrorCS", {"start": v(0, -90) * mm, "end": v(0, -120) * mm, "construction": true});
            skSolve(sketch);
        }
        {
            var Q0;
            {var subQ0=sQuery(id+"F16.wireOp",EDGE,"E80");Q0=makeQuery(id+"F16.imprint","IMPRINT",FACE,{"disambiguationData":[TD([[makeQuery(id+"F16.imprint","IMPRINT",EDGE,{"derivedFrom":subQ0}),-1.0]])]});}
            var Q1;
            Q1=makeQuery(id+"F16.imprint","IMPRINT",FACE,{"disambiguationData":[TD([[makeQuery(id+"F16.imprint","IMPRINT",EDGE,{"derivedFrom":sQuery(id+"F16.wireOp",EDGE,"E87.MirrorC")}),1.0]])]});
            var Q2;
            Q2=makeQuery(id+"F16.imprint","IMPRINT",FACE,{"disambiguationData":[TD([[makeQuery(id+"F16.imprint","IMPRINT",EDGE,{"derivedFrom":makeQuery(id+"F1.opExtrude","CAP_EDGE",EDGE,{"disambiguationData":[OSD([sQuery(id+"F0.wireOp",EDGE,"E1.left")])],"isStart":true})}),-1.0]])]});
            var Q3;
            Q3=makeQuery(id+"F2.opExtrude","CAP_FACE",FACE,{"disambiguationData":[OSD([sQuery(id+"F0.wireOp",EDGE,"E12"),sQuery(id+"F0.wireOp",EDGE,"E13"),sQuery(id+"F0.wireOp",EDGE,"E14"),sQuery(id+"F0.wireOp",EDGE,"E15"),sQuery(id+"F0.wireOp",EDGE,"E17.filletArc"),sQuery(id+"F0.wireOp",EDGE,"E18.filletArc"),sQuery(id+"F0.wireOp",EDGE,"E19.filletArc"),sQuery(id+"F0.wireOp",EDGE,"E20.filletArc"),sQuery(id+"F0.wireOp",EDGE,"E25.0"),sQuery(id+"F0.wireOp",EDGE,"E25.1"),sQuery(id+"F0.wireOp",EDGE,"E25.2"),sQuery(id+"F0.wireOp",EDGE,"E25.3"),sQuery(id+"F0.wireOp",EDGE,"E25.4"),sQuery(id+"F0.wireOp",EDGE,"E25.5"),sQuery(id+"F0.wireOp",EDGE,"E25.6"),sQuery(id+"F0.wireOp",EDGE,"E25.7")])],"isStart":false});
            extrude(context, id + "F17", {"entities" : qUnion([Q0, Q1, Q2]), "endBound" : BoundingType.UP_TO_SURFACE, "depth" : 25 * mm, "endBoundEntityFace" : qUnion([Q3]), "offsetDistance" : 25 * mm});
        }
    });
